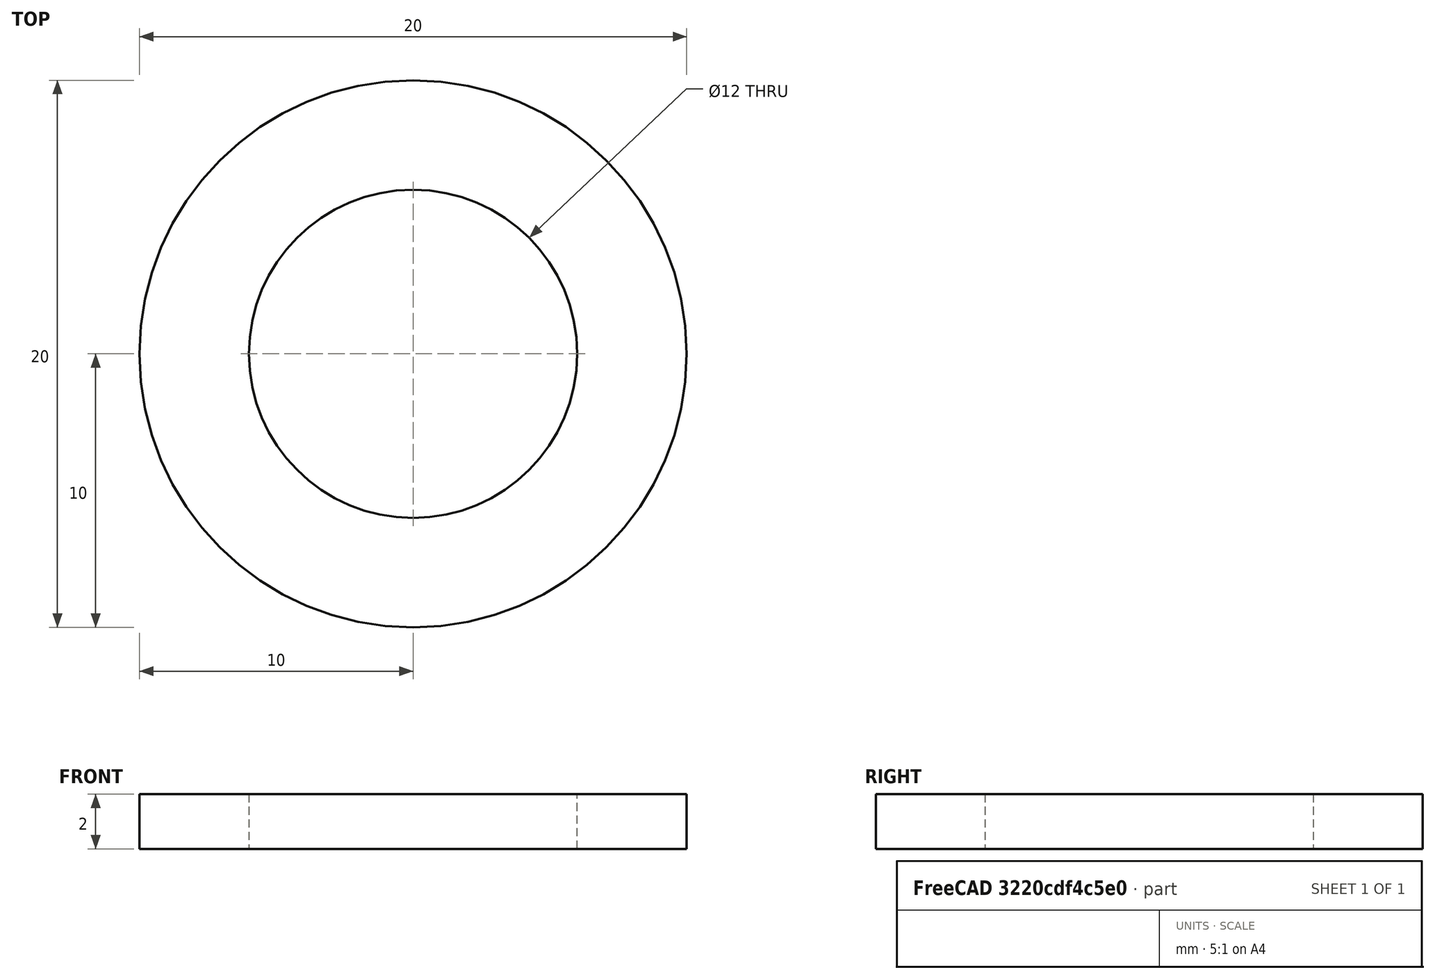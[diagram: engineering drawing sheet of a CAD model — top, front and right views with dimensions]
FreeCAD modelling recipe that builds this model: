
FCSTD DOCUMENT  (FreeCAD 0.21R33771 (Git))
Label: end_limit_washer
License: All rights reserved
LicenseURL: https://en.wikipedia.org/wiki/All_rights_reserved
objects: Sketcher::SketchObject×1, PartDesign::Pad×1, PartDesign::Body×1, Mesh::Feature×1
note: 4 computed .brp shape members not serialized (recipe doc carries the construction recipe); baked Part::Feature solids carry a one-line shape summary decoded from their .brp

FEATURE [Sketcher::SketchObject] Sketch
  FullyConstrained = true
  MapMode = 5
  Support = -> [XY_Plane]
  sketch-geometry (2):
    g0: Circle CenterX=0 CenterY=0 CenterZ=0 NormalX=0 NormalY=0 NormalZ=1 AngleXU=0 Radius=10
    g1: Circle CenterX=0 CenterY=0 CenterZ=0 NormalX=0 NormalY=0 NormalZ=1 AngleXU=0 Radius=6
  constraints (4):
    c: Coincident(g0,g-1)
    c: Diameter(g0) = 20
    c: Coincident(g1,g0)
    c: Diameter(g1) = 12
FEATURE [PartDesign::Pad] Pad
  Direction = (0,0,1)
  Length = 2
  Length2 = 10
  Profile = -> Sketch
  ReferenceAxis = -> Sketch [N_Axis]
  Type = 0
FEATURE [PartDesign::Body] Body
  Group = -> [Sketch,Pad]
  Origin = -> Origin
  Tip = -> Pad
FEATURE [Mesh::Feature] Mesh  label="Body (Meshed)"
